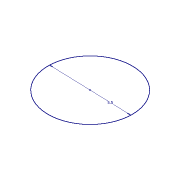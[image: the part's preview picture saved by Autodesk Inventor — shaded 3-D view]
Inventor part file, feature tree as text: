
AUTODESK INVENTOR PART (.ipt)
format: ipt  version: 2015 (Build 190159000, 159)  size: 55,808 bytes
history: native  units: mm
features: sketch x1
ambient origin geometry x8: Origin, YZ Plane, XZ Plane, XY Plane, X Axis, Y Axis, Z Axis, Center Point
feature tree (1):
  sketch  "Sketch1"  dims[d0=5.5mm]
